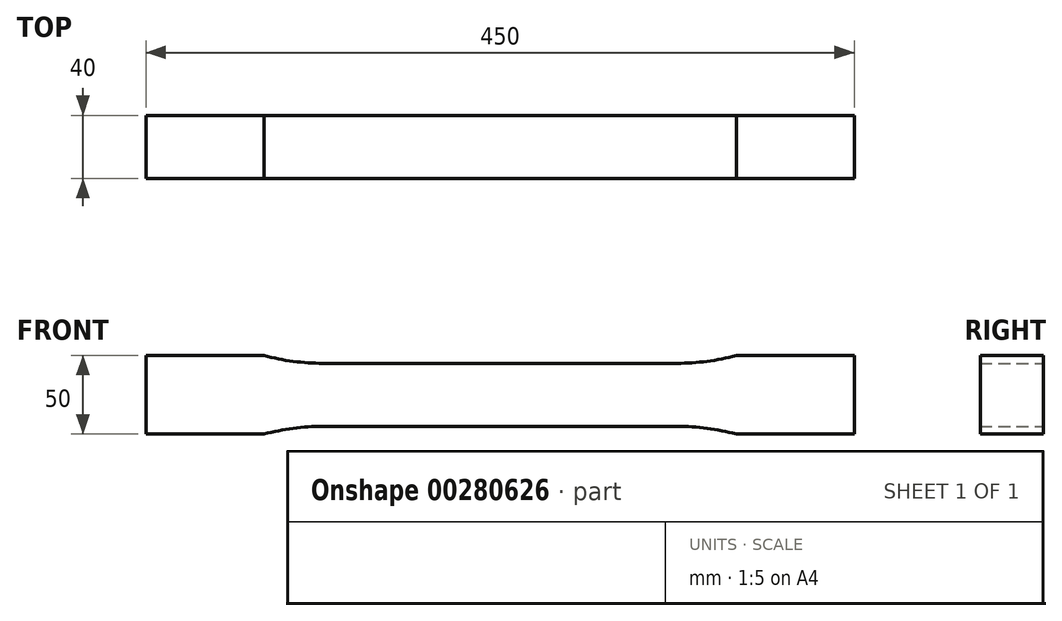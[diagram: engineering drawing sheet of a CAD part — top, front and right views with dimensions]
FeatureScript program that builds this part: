
annotation { "Feature Type Name" : "Feature", "Feature Type Description" : "" }
export const myFeature = defineFeature(function(context is Context, id is Id, definition is map)
    precondition{}
    {
        {
            var Q0;
            Q0=qCreatedBy(makeId("Front.planeOp"),FACE);
            var sketch = newSketch(context, id + "F0", { "sketchPlane" : qUnion([Q0])});
            skLineSegment(sketch, "E0", {"start": v(112.5, 20) * mm, "end": v(0, 20) * mm});
            skArc(sketch, "E1", {"start": v(112.5, 20) * mm, "mid": v(131.42, 21.26) * mm, "end": v(150, 25) * mm});
            skLineSegment(sketch, "E2", {"start": v(150, 25) * mm, "end": v(225, 25) * mm});
            skLineSegment(sketch, "E3", {"start": v(225, 25) * mm, "end": v(225, 0) * mm});
            skLineSegment(sketch, "E4.MirrorCS", {"start": v(112.5, -20) * mm, "end": v(0, -20) * mm});
            skArc(sketch, "E5.MirrorCS", {"start": v(112.5, -20) * mm, "mid": v(131.42, -21.26) * mm, "end": v(150, -25) * mm});
            skLineSegment(sketch, "E6.MirrorCS", {"start": v(150, -25) * mm, "end": v(225, -25) * mm});
            skLineSegment(sketch, "E7.MirrorCS", {"start": v(225, -25) * mm, "end": v(225, 0) * mm});
            skLineSegment(sketch, "E8.MirrorCS", {"start": v(-112.5, 20) * mm, "end": v(0, 20) * mm});
            skArc(sketch, "E9.MirrorCS", {"start": v(-112.5, 20) * mm, "mid": v(-131.42, 21.26) * mm, "end": v(-150, 25) * mm});
            skLineSegment(sketch, "E10.MirrorCS", {"start": v(-150, 25) * mm, "end": v(-225, 25) * mm});
            skLineSegment(sketch, "E11.MirrorCS", {"start": v(-225, 25) * mm, "end": v(-225, 0) * mm});
            skLineSegment(sketch, "E12.MirrorCS", {"start": v(-225, -25) * mm, "end": v(-225, 0) * mm});
            skLineSegment(sketch, "E13.MirrorCS", {"start": v(-150, -25) * mm, "end": v(-225, -25) * mm});
            skArc(sketch, "E14.MirrorCS", {"start": v(-112.5, -20) * mm, "mid": v(-131.42, -21.26) * mm, "end": v(-150, -25) * mm});
            skLineSegment(sketch, "E15.MirrorCS", {"start": v(-112.5, -20) * mm, "end": v(0, -20) * mm});
            skSolve(sketch);
        }
        {
            var Q0;
            Q0 = qSketchRegion(id + "F0", true);
            extrude(context, id + "F1", {"entities" : qUnion([Q0]), "endBound" : BoundingType.SYMMETRIC, "depth" : 40 * mm});
        }
    });
